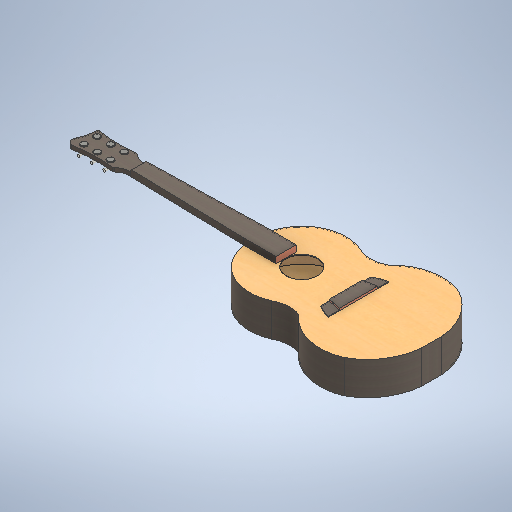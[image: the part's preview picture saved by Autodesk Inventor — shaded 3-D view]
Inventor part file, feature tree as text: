
AUTODESK INVENTOR PART (.ipt)
format: ipt  version: 2025.2 (Build 292293000, 293)  size: 949,248 bytes
history: native  units: in
note: dims shown in document units (in); Inventor stores cm internally (conversion verified against a paired STEP export)
features: extrude x11, sketch x11, plane x5, fillet x4, shell x1
ambient origin geometry x8: Origin, YZ Plane, XZ Plane, XY Plane, X Axis, Y Axis, Z Axis, Center Point
bodies: Solid1 (feature_tree)
feature tree (32):
  extrude  "Extrusion1"  Depth=0.5118in
  fillet  "Fillet3"  Radius=0.5118in
  extrude  "Extrusion3"  Depth=4.3307in
  fillet  "Fillet5"  Radius=4.3307in
  plane  "Work Plane2"
  extrude  "Extrusion4"  Depth=0.1181in
  plane  "Work Plane4"
  extrude  "Extrusion5"  Depth=13.7795in
  extrude  "Extrusion6"  Depth=0.3937in TaperAngle=0.0deg
  plane  "Work Plane3"
  extrude  "Extrusion7"  Depth=12.4016in
  extrude  "Extrusion8"  Depth=0.1575in
  fillet  "Fillet7"  Radius=0.1575in
  extrude  "Extrusion9"  Depth=2.1654in
  extrude  "Extrusion10"  Depth=0.0787in
  fillet  "Fillet8"  Radius=5.5118in
  plane  "Work Plane5"
  extrude  "Extrusion11"  Depth=2.7559in
  plane  "Work Plane6"
  extrude  "Extrusion12"  Depth=2.7559in
  shell  "Shell2"  Thickness=3.1496in
  sketch  "Sketch1"  dims[d7=1.378in d8=0.5118in d9=0.5118in]
  sketch  "Sketch3"  dims[d10=1.378in d11=4.3307in d12=4.3307in]
  sketch  "Sketch4"  dims[d13=1.5748in d14=0.1181in]
  sketch  "Sketch5"  dims[d15=0.1181in d16=13.7795in]
  sketch  "Sketch6"  dims[d17=13.7795in d18=0.3937in d19=0.0in]
  sketch  "Sketch7"  dims[d30=12.4016in d31=1.5748in]
  sketch  "Sketch8"  dims[d32=0.2953in d33=0.2953in d34=0.1575in]
  sketch  "Sketch10"  dims[d39=3.4252in d41=2.1654in]
  sketch  "Sketch11"  dims[d42=0.2756in d43=0.0in d44=0.0787in d58=5.5118in]
  sketch  "Sketch12"  dims[d59=5.5118in d63=2.7559in]
  sketch  "Sketch13"  dims[d64=3.1496in d65=2.7559in d66=3.1496in d67=4.7244in d68=4.7244in d69=3.5433in d70=0.0in d71=3.3465in d72=1.6732in d74=2.1654in d75=6.2992in d76=6.2992in d77=0.0in d78=0.0in d79=0.6051in d80=0.6051in d81=1.0579in d82=1.0579in d83=0.0in d84=0.4501in d85=0.4501in d86=3.1496in d87=0.0in d90=1.378in d91=3.5433in d92=4.7047in d94=0.2756in d95=0.2756in d96=0.2362in d97=0.0in d98=0.9055in d99=1.1811in d100=4.7244in d101=0.9055in d102=1.1811in d103=4.7244in d104=0.0787in d105=0.0in d114=0.7087in d116=0.7874in d117=0.3949in d118=0.1563in d119=0.7087in d120=0.7087in d121=1.4173in d122=1.4567in d123=0.7372in d124=0.0787in d125=0.0in d126=0.0394in d128=4.3307in d129=0.5118in d130=0.0039in d131=0.0in d132=0.3937in d133=0.0394in d134=0.3543in d135=0.3937in d136=0.0394in d137=0.3937in d138=0.0394in d139=0.9843in d140=0.9843in d141=0.3937in d142=0.0in d143=0.0394in d144=0.2756in d145=0.1969in d146=0.1969in d147=0.2756in d148=0.2756in d149=0.1969in d150=0.1969in d151=0.1969in d152=0.1969in d153=1.1811in d154=0.0in d155=0.2756in d156=0.2756in d157=0.2756in d158=0.1969in d159=0.1969in d160=0.1969in d161=0.1969in d162=0.1969in d163=0.1969in d164=1.1811in d165=0.0in d166=0.0787in d88=0.0197in d89=0.0344in]
